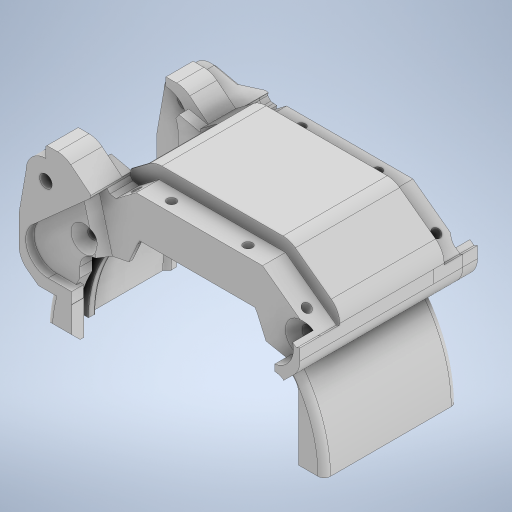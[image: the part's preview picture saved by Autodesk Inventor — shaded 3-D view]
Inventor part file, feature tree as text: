
AUTODESK INVENTOR PART (.ipt)
format: ipt  version: 2023.4 (Build 274418000, 418)  size: 1,996,288 bytes
history: native  units: mm
features: extrude x60, sketch x60, projected_geometry x49, chamfer x16, thicken_offset x6, fillet x4, plane x2
ambient origin geometry x8: Origin, YZ Plane, XZ Plane, XY Plane, X Axis, Y Axis, Z Axis, Center Point
bodies: Solid1 (feature_tree)
feature tree (197):
  extrude  "Extrusion1"  Depth=2.0mm
  extrude  "Extrusion2"  Depth=122.0mm
  extrude  "Extrusion3"  Depth=4.6mm TaperAngle=0.0deg
  extrude  "Extrusion4"  Depth=2.0mm TaperAngle=0.0deg
  extrude  "Extrusion5"  Depth=0.1mm
  thicken_offset  "Thicken1"
  thicken_offset  "Thicken2"
  extrude  "Extrusion6"  Depth=0.1mm
  extrude  "Extrusion7"  Depth=7.0mm TaperAngle=0.0deg
  extrude  "Extrusion8"  Depth=10.0mm TaperAngle=0.0deg
  extrude  "Extrusion9"  Depth=9.0mm TaperAngle=0.0deg
  extrude  "Extrusion10"  Depth=10.0mm TaperAngle=0.0deg
  extrude  "Extrusion11"  Depth=15.0mm TaperAngle=0.0deg
  extrude  "Extrusion12"  Depth=3.0mm
  sketch  "Sketch13"  dims[d40=4.0mm d41=0.0mm d42=12.0mm d43=0.0mm]
  plane  "Work Plane1"
  extrude  "Extrusion13"  Depth=12.0mm TaperAngle=0.0deg
  extrude  "Extrusion14"  Depth=3.0mm TaperAngle=0.0deg
  extrude  "Extrusion15"  Depth=5.0mm TaperAngle=0.0deg
  extrude  "Extrusion16"  Depth=1.0mm TaperAngle=0.0deg
  extrude  "Extrusion17"  Depth=4.0mm TaperAngle=0.0deg
  extrude  "Extrusion18"  Depth=10.0mm TaperAngle=0.0deg
  extrude  "Extrusion19"  Depth=3.0mm TaperAngle=0.0deg
  extrude  "Extrusion20"  Depth=10.0mm TaperAngle=0.0deg
  extrude  "Extrusion21"  Depth=1.3mm TaperAngle=45.0deg
  extrude  "Extrusion22"  Depth=10.0mm TaperAngle=0.0deg
  extrude  "Extrusion23"  Depth=3.0mm TaperAngle=0.0deg
  extrude  "Extrusion24"  Depth=3.0mm TaperAngle=45.0deg
  extrude  "Extrusion25"  Depth=3.0mm TaperAngle=0.0deg
  extrude  "Extrusion28"  Depth=10.0mm
  extrude  "Extrusion29"  Depth=4.0mm TaperAngle=45.0deg
  fillet  "Fillet2"  Radius=4.0mm
  extrude  "Extrusion30"  Depth=4.25mm
  extrude  "Extrusion31"  Depth=4.25mm
  extrude  "Extrusion32"  Depth=4.25mm
  chamfer  "Chamfer4"  Distance=9.0mm
  chamfer  "Chamfer5"  Distance=9.0mm
  chamfer  "Chamfer6"  Distance=6.0mm
  extrude  "Extrusion33"  Depth=6.0mm TaperAngle=0.0deg
  extrude  "Extrusion34"  Depth=4.0mm TaperAngle=0.0deg
  extrude  "Extrusion35"  Depth=30.0mm
  chamfer  "Chamfer7"  Distance=32.5mm
  extrude  "Extrusion36"  TaperAngle=0.0deg  [1 undecoded]
  extrude  "Extrusion37"  Depth=0.2mm
  extrude  "Extrusion38"  Depth=3.0mm TaperAngle=0.0deg
  chamfer  "Chamfer8"  Distance=2.0mm
  chamfer  "Chamfer9"  Distance=4.0mm Angle=45.0deg
  chamfer  "Chamfer10"  Distance=4.0mm Angle=45.0deg
  extrude  "Extrusion39"  Depth=10.0mm
  extrude  "Extrusion40"  Depth=0.2mm
  extrude  "Extrusion41"  Depth=0.2mm
  extrude  "Extrusion42"  Depth=3.0mm TaperAngle=0.0deg
  extrude  "Extrusion43"  Depth=3.0mm TaperAngle=0.0deg
  extrude  "Extrusion44"  Depth=4.0mm TaperAngle=45.0deg
  extrude  "Extrusion45"  Depth=4.5mm
  extrude  "Extrusion46"  Depth=2.5mm
  extrude  "Extrusion47"  Depth=10.0mm TaperAngle=45.0deg
  plane  "Work Plane2"
  extrude  "Extrusion48"  Depth=10.0mm TaperAngle=0.0deg
  extrude  "Extrusion50"  Depth=10.0mm TaperAngle=0.0deg
  extrude  "Extrusion51"  Depth=4.0mm TaperAngle=45.0deg
  thicken_offset  "Thicken3"
  extrude  "Extrusion52"  Depth=3.0mm
  extrude  "Extrusion53"  [1 undecoded]
  extrude  "Extrusion54"  [1 undecoded]
  chamfer  "Chamfer13"  [1 undecoded]
  chamfer  "Chamfer14"  [1 undecoded]
  chamfer  "Chamfer15"  [1 undecoded]
  fillet  "Fillet3"  [1 undecoded]
  thicken_offset  "Thicken4"
  thicken_offset  "Thicken5"
  thicken_offset  "Thicken6"
  extrude  "Extrusion55"  [1 undecoded]
  extrude  "Extrusion56"  [1 undecoded]
  extrude  "Extrusion57"  [1 undecoded]
  chamfer  "Chamfer16"  [1 undecoded]
  chamfer  "Chamfer17"  [1 undecoded]
  chamfer  "Chamfer18"  [1 undecoded]
  extrude  "Extrusion58"  [1 undecoded]
  extrude  "Extrusion59"  [1 undecoded]
  chamfer  "Chamfer19"  [1 undecoded]
  extrude  "Extrusion60"  [1 undecoded]
  extrude  "Extrusion61"  [1 undecoded]
  extrude  "Extrusion62"  [1 undecoded]
  extrude  "Extrusion63"  [1 undecoded]
  chamfer  "Chamfer21"  [1 undecoded]
  chamfer  "Chamfer22"  [1 undecoded]
  fillet  "Fillet4"  [1 undecoded]
  fillet  "Fillet5"  [1 undecoded]
  sketch  "Sketch1"  dims[d0=125.0mm d1=2.0mm]
  sketch  "Sketch2"  dims[d2=4.6mm d3=0.0mm d4=122.0mm]
  sketch  "Sketch3"  dims[d5=42.8mm d6=0.0mm d7=4.6mm d8=0.0mm]
  projected_geometry  "Projected Loop1"
  sketch  "Sketch4"  dims[d10=2.0mm d11=0.0mm d12=2.0mm d13=0.0mm]
  sketch  "Sketch5"  dims[d14=0.1mm d15=0.1mm]
  projected_geometry  "Projected Loop2"
  projected_geometry  "Projected Loop3"
  sketch  "Sketch6"  dims[d16=0.1mm d17=0.1mm]
  projected_geometry  "Projected Loop4"
  sketch  "Sketch7"  dims[d18=0.0mm d19=0.0mm d20=7.0mm d21=0.0mm]
  projected_geometry  "Projected Loop5"
  sketch  "Sketch8"  dims[d22=0.0mm d23=0.0mm d24=10.0mm d25=0.0mm]
  projected_geometry  "Projected Loop6"
  projected_geometry  "Projected Loop7"
  sketch  "Sketch9"  dims[d26=9.0mm d27=0.0mm d28=9.0mm d29=0.0mm]
  projected_geometry  "Projected Loop8"
  sketch  "Sketch10"  dims[d30=10.0mm d31=0.0mm d32=10.0mm d33=0.0mm]
  sketch  "Sketch11"  dims[d34=15.0mm d35=0.0mm d36=15.0mm d37=0.0mm]
  projected_geometry  "Projected Loop9"
  sketch  "Sketch12"  dims[d38=3.0mm d39=3.0mm]
  projected_geometry  "Projected Loop10"
  sketch  "Sketch14"  dims[d44=3.0mm d45=0.0mm d46=7.0mm d47=0.0mm]
  projected_geometry  "Projected Loop11"
  projected_geometry  "Projected Loop12"
  sketch  "Sketch15"  dims[d48=2.0mm d49=0.0mm d50=5.0mm d51=0.0mm]
  sketch  "Sketch16"  dims[d52=5.0mm d53=0.0mm d54=1.0mm d55=0.0mm]
  projected_geometry  "Projected Loop13"
  sketch  "Sketch17"  dims[d56=4.0mm d57=0.0mm d58=4.0mm d59=0.0mm]
  sketch  "Sketch18"  dims[d74=10.0mm d75=0.0mm d76=3.9mm d77=0.0mm]
  projected_geometry  "Projected Loop14"
  sketch  "Sketch19"  dims[d78=3.0mm d79=15.0mm d80=0.0mm]
  sketch  "Sketch20"  dims[d81=15.0mm d82=0.0mm d83=10.0mm d84=0.0mm]
  projected_geometry  "Projected Loop15"
  sketch  "Sketch21"  dims[d85=4.0mm d86=2.0mm d87=45.0deg d88=1.3mm d89=2.0mm d90=45.0deg]
  projected_geometry  "Projected Loop16"
  sketch  "Sketch22"  dims[d91=3.0mm d92=2.0mm d93=45.0deg d94=10.0mm d95=0.0mm]
  projected_geometry  "Projected Loop17"
  projected_geometry  "Projected Loop18"
  projected_geometry  "Projected Loop19"
  projected_geometry  "Projected Loop20"
  projected_geometry  "Projected Loop21"
  projected_geometry  "Projected Loop22"
  projected_geometry  "Projected Loop23"
  projected_geometry  "Projected Loop24"
  projected_geometry  "Projected Loop25"
  projected_geometry  "Projected Loop26"
  sketch  "Sketch24"  dims[d96=2.0mm d97=3.0mm d98=0.0mm]
  projected_geometry  "Projected Loop28"
  sketch  "Sketch25"  dims[d99=3.0mm d100=0.0mm d101=2.0mm d102=2.0mm d103=45.0deg]
  sketch  "Sketch26"  dims[d104=6.0mm d105=3.0mm d106=0.0mm]
  sketch  "Sketch29"  dims[d107=10.0mm d108=0.0mm d109=11.2mm]
  projected_geometry  "Projected Loop31"
  sketch  "Sketch30"  dims[d110=6.0mm d111=0.0mm d112=4.0mm d113=2.0mm d114=45.0deg]
  projected_geometry  "Projected Loop32"
  sketch  "Sketch31"  dims[d115=2.0mm d116=2.0mm d117=45.0deg]
  sketch  "Sketch32"  dims[d118=1.0mm d119=2.0mm d120=45.0deg d121=4.0mm d122=0.0mm]
  sketch  "Sketch33"  dims[d123=4.25mm d124=4.25mm]
  sketch  "Sketch34"  dims[d125=4.25mm d126=4.25mm]
  sketch  "Sketch35"  dims[d127=9.0mm d128=0.0mm d129=4.25mm]
  sketch  "Sketch36"  dims[d130=4.25mm d131=9.0mm d132=0.0mm]
  projected_geometry  "Projected Loop33"
  sketch  "Sketch37"  dims[d133=4.25mm]
  projected_geometry  "Projected Loop34"
  sketch  "Sketch38"  dims[d134=4.25mm d135=9.0mm d136=0.0mm d137=6.0mm d138=0.0mm]
  projected_geometry  "Projected Loop35"
  sketch  "Sketch39"  dims[d139=6.0mm d140=0.0mm d141=6.0mm d142=0.0mm]
  sketch  "Sketch40"  dims[d143=9.0mm d144=0.0mm d145=4.0mm d146=0.0mm]
  projected_geometry  "Projected Loop36"
  sketch  "Sketch41"  dims[d147=-5.0mm d148=30.0mm d149=32.5mm d150=0.0mm]
  sketch  "Sketch42"  dims[d153=10.0mm d154=0.0mm d158=0.0mm d159=0.0mm]
  sketch  "Sketch43"  dims[d163=0.2mm d164=0.2mm]
  sketch  "Sketch44"  dims[d165=3.0mm d166=0.0mm d167=2.0mm d168=0.0mm d169=2.0mm d170=0.0mm d171=4.0mm d172=2.0mm d173=45.0deg d174=4.0mm d175=2.0mm d176=45.0deg]
  sketch  "Sketch45"  dims[d177=0.5mm d178=2.0mm d179=45.0deg d180=10.0mm]
  projected_geometry  "Projected Loop37"
  sketch  "Sketch46"  dims[d181=0.2mm d182=0.2mm]
  projected_geometry  "Projected Loop38"
  sketch  "Sketch47"  dims[d183=0.2mm d184=0.2mm d185=0.2mm]
  projected_geometry  "Projected Loop39"
  sketch  "Sketch48"  dims[d186=0.2mm d187=3.0mm d188=0.0mm]
  projected_geometry  "Projected Loop40"
  sketch  "Sketch49"  dims[d189=3.0mm d190=0.0mm d191=5.0mm d192=0.0mm]
  sketch  "Sketch51"  dims[d193=4.0mm d194=2.0mm d195=45.0deg d196=4.0mm d197=2.0mm d198=45.0deg]
  projected_geometry  "Projected Loop41"
  sketch  "Sketch52"  dims[d199=4.0mm d200=2.0mm d201=45.0deg d202=4.5mm]
  sketch  "Sketch53"  dims[d203=0.0mm d204=0.0mm d205=2.5mm]
  projected_geometry  "Projected Loop42"
  sketch  "Sketch54"  dims[d206=10.0mm d207=0.0mm d208=4.0mm d209=2.0mm d210=45.0deg]
  projected_geometry  "Projected Loop43"
  projected_geometry  "Projected Loop44"
  sketch  "Sketch55"  dims[d211=10.0mm d212=0.0mm d216=5.0mm d217=0.0mm]
  projected_geometry  "Projected Loop45"
  projected_geometry  "Projected Loop46"
  sketch  "Sketch56"  dims[d218=5.0mm d219=0.0mm d220=10.0mm d221=0.0mm]
  projected_geometry  "Projected Loop47"
  sketch  "Sketch57"  dims[d222=4.0mm d223=2.0mm d224=45.0deg d225=4.0mm d226=2.0mm d227=45.0deg]
  projected_geometry  "Projected Loop48"
  sketch  "Sketch58"  dims[d228=3.0mm d229=3.0mm]
  projected_geometry  "Projected Loop49"
  sketch  "Sketch59"  dims[d9=0.5mm]
  sketch  "Sketch60"
  sketch  "Sketch61"
  sketch  "Sketch62"
  projected_geometry  "Projected Loop50"
  sketch  "Sketch63"
  sketch  "Sketch64"
  projected_geometry  "Projected Loop51"
  projected_geometry  "Projected Loop52"
note: 24 required parameter values undecoded (feature->parameter linkage not recoverable at this tier; creation-order binding heuristic only, values carry confidence <= 0.55)
